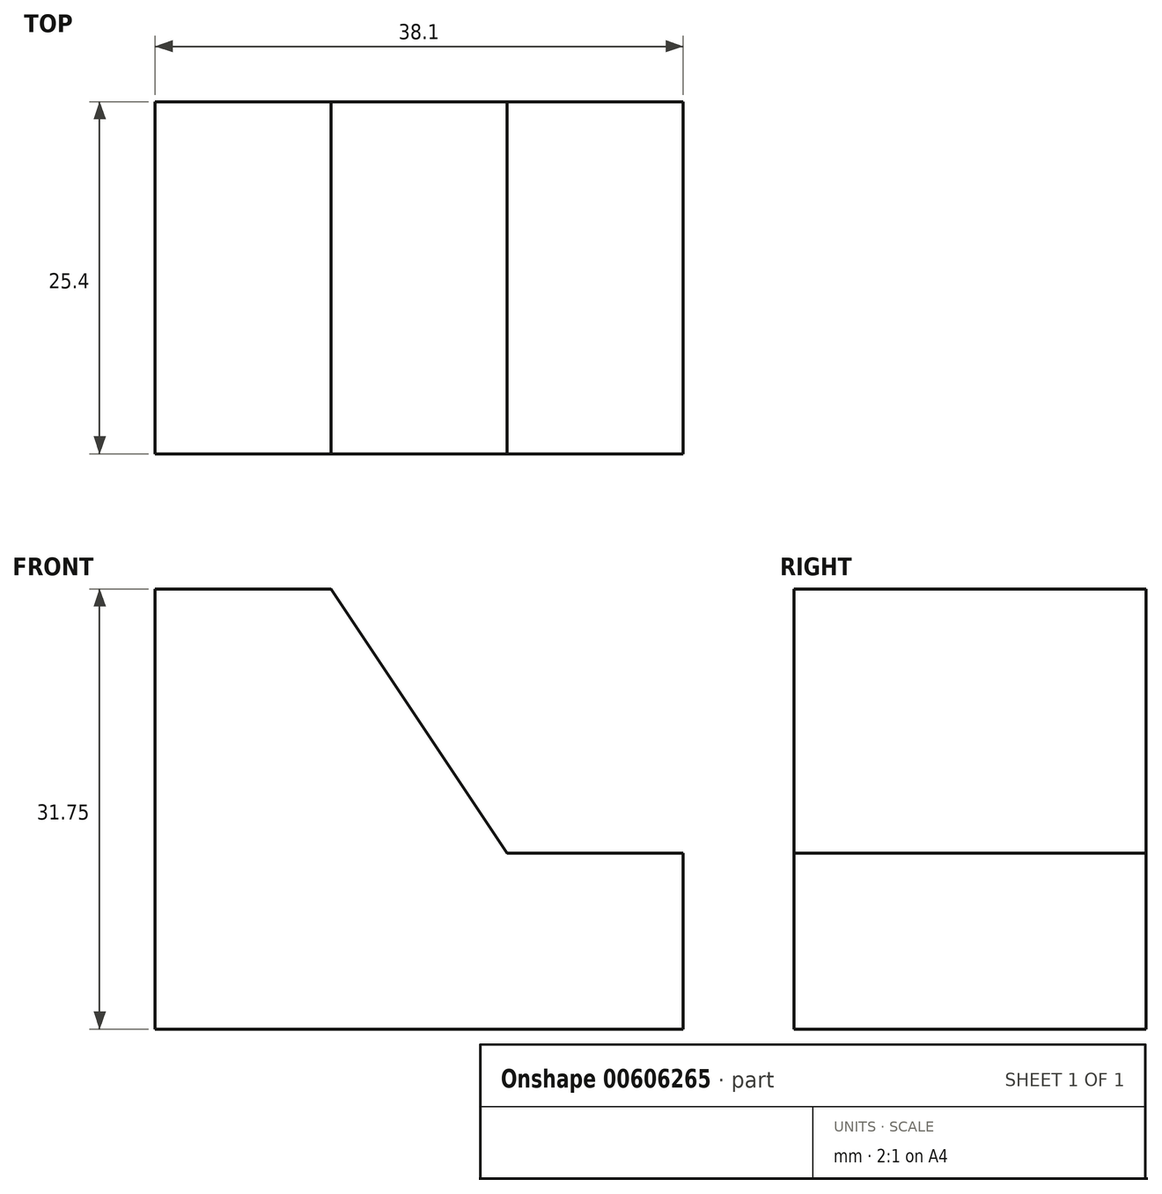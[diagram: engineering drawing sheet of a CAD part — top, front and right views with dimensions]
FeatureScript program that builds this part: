
annotation { "Feature Type Name" : "Feature", "Feature Type Description" : "" }
export const myFeature = defineFeature(function(context is Context, id is Id, definition is map)
    precondition{}
    {
        {
            var Q0;
            Q0=qCreatedBy(makeId("Front.planeOp"),FACE);
            var sketch = newSketch(context, id + "F0", { "sketchPlane" : qUnion([Q0])});
            skLineSegment(sketch, "E0", {"start": v(0, 0) * mm, "end": v(0, 31.75) * mm});
            skLineSegment(sketch, "E1", {"start": v(0, 31.75) * mm, "end": v(12.7, 31.75) * mm});
            skLineSegment(sketch, "E2", {"start": v(0, 0) * mm, "end": v(10.03, 0) * mm});
            skLineSegment(sketch, "E3", {"start": v(0, 0) * mm, "end": v(38.1, 0) * mm});
            skPoint(sketch, "E3.endSnap0", {"position": v(5.01, 0) * mm});
            skLineSegment(sketch, "E4", {"start": v(38.1, 0) * mm, "end": v(38.1, 12.7) * mm});
            skLineSegment(sketch, "E5", {"start": v(38.1, 12.7) * mm, "end": v(25.4, 12.7) * mm});
            skLineSegment(sketch, "E6", {"start": v(12.7, 31.75) * mm, "end": v(25.4, 12.7) * mm});
            skSolve(sketch);
        }
        {
            var Q0;
            {var subQ2=sQuery(id+"F0.wireOp",EDGE,"E0");Q0=makeQuery(id+"F0.imprint","IMPRINT",FACE,{"disambiguationData":[TD([[makeQuery(id+"F0.imprint","IMPRINT",EDGE,{"derivedFrom":subQ2}),-1.0]])]});}
            extrude(context, id + "F1", {"entities" : qUnion([Q0]), "depth" : 25.4 * mm, "offsetDistance" : 25.4 * mm});
        }
    });
